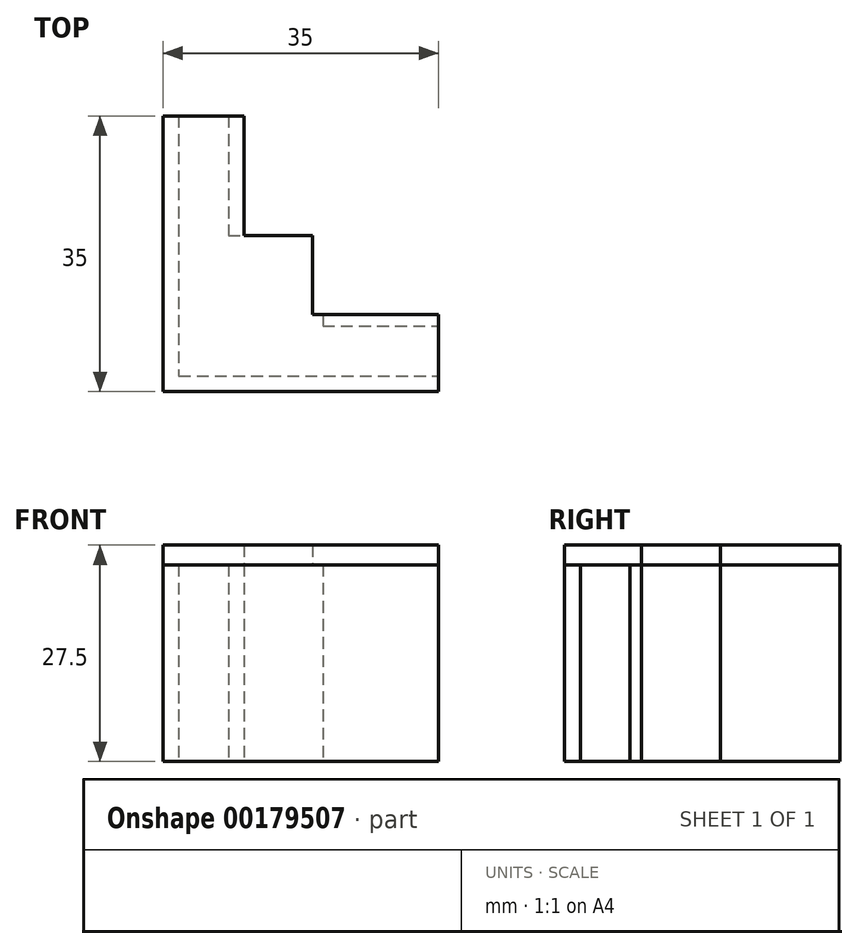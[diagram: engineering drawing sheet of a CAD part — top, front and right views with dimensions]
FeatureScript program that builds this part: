
annotation { "Feature Type Name" : "Feature", "Feature Type Description" : "" }
export const myFeature = defineFeature(function(context is Context, id is Id, definition is map)
    precondition{}
    {
        {
            var Q0;
            Q0=qCreatedBy(makeId("Top.planeOp"),FACE);
            var sketch = newSketch(context, id + "F0", { "sketchPlane" : qUnion([Q0])});
            skLineSegment(sketch, "E0", {"start": v(-10.3, 25.2) * mm, "end": v(-10.3, -9.8) * mm});
            skLineSegment(sketch, "E1", {"start": v(-10.3, -9.8) * mm, "end": v(24.7, -9.8) * mm});
            skLineSegment(sketch, "E2", {"start": v(24.7, -9.8) * mm, "end": v(24.7, -7.8) * mm});
            skLineSegment(sketch, "E3", {"start": v(24.7, 0) * mm, "end": v(10, 0) * mm});
            skLineSegment(sketch, "E4", {"start": v(0, 10) * mm, "end": v(0, 25.2) * mm});
            skLineSegment(sketch, "E5", {"start": v(0, 25.2) * mm, "end": v(-2, 25.2) * mm});
            skLineSegment(sketch, "E6", {"start": v(-2, 25.2) * mm, "end": v(-2, 10) * mm});
            skLineSegment(sketch, "E7", {"start": v(10, -1.5) * mm, "end": v(24.7, -1.5) * mm});
            skLineSegment(sketch, "E8", {"start": v(-8.3, 25.2) * mm, "end": v(-8.3, -7.8) * mm});
            skLineSegment(sketch, "E9", {"start": v(-8.3, -7.8) * mm, "end": v(24.7, -7.8) * mm});
            skPoint(sketch, "E10.orphan", {"position": v(0, 0) * mm});
            skLineSegment(sketch, "E11.trimOffspring", {"start": v(-8.3, 25.2) * mm, "end": v(-10.3, 25.2) * mm});
            skLineSegment(sketch, "E12.trimOffspring", {"start": v(24.7, -1.5) * mm, "end": v(24.7, 0) * mm});
            skLineSegment(sketch, "E13", {"start": v(-2, 10) * mm, "end": v(0, 10) * mm});
            skLineSegment(sketch, "E14", {"start": v(10, 0) * mm, "end": v(10, -1.5) * mm});
            skSolve(sketch);
        }
        {
            var Q0;
            Q0 = qSketchRegion(id + "F0", true);
            extrude(context, id + "F1", {"entities" : qUnion([Q0]), "depth" : 25 * mm});
        }
        {
            var Q0;
            Q0=makeQuery(id+"F1.opExtrude","CAP_FACE",FACE,{"disambiguationData":[OSD([sQuery(id+"F0.wireOp",EDGE,"E0"),sQuery(id+"F0.wireOp",EDGE,"E1"),sQuery(id+"F0.wireOp",EDGE,"E2"),sQuery(id+"F0.wireOp",EDGE,"E8"),sQuery(id+"F0.wireOp",EDGE,"E9"),sQuery(id+"F0.wireOp",EDGE,"E11.trimOffspring")])],"isStart":false});
            var sketch = newSketch(context, id + "F2", { "sketchPlane" : qUnion([Q0])});
            skLineSegment(sketch, "E15", {"start": v(-10.3, 25.2) * mm, "end": v(0, 25.2) * mm});
            skLineSegment(sketch, "E16.1", {"start": v(0, 10) * mm, "end": v(0, 25.2) * mm});
            skLineSegment(sketch, "E16.2", {"start": v(0, 10) * mm, "end": v(8.7, 10) * mm});
            skLineSegment(sketch, "E16.3", {"start": v(8.7, 10) * mm, "end": v(8.7, 0) * mm});
            skLineSegment(sketch, "E16.4", {"start": v(24.7, 0) * mm, "end": v(8.7, 0) * mm});
            skLineSegment(sketch, "E16.5", {"start": v(-10.3, 25.2) * mm, "end": v(-10.3, -9.8) * mm});
            skLineSegment(sketch, "E16.6", {"start": v(-10.3, -9.8) * mm, "end": v(24.7, -9.8) * mm});
            skLineSegment(sketch, "E17", {"start": v(24.7, 0) * mm, "end": v(24.7, -9.8) * mm});
            skSolve(sketch);
        }
        {
            var Q0;
            Q0 = qSketchRegion(id + "F2", true);
            extrude(context, id + "F3", {"entities" : qUnion([Q0]), "depth" : 2.5 * mm});
        }
    });
